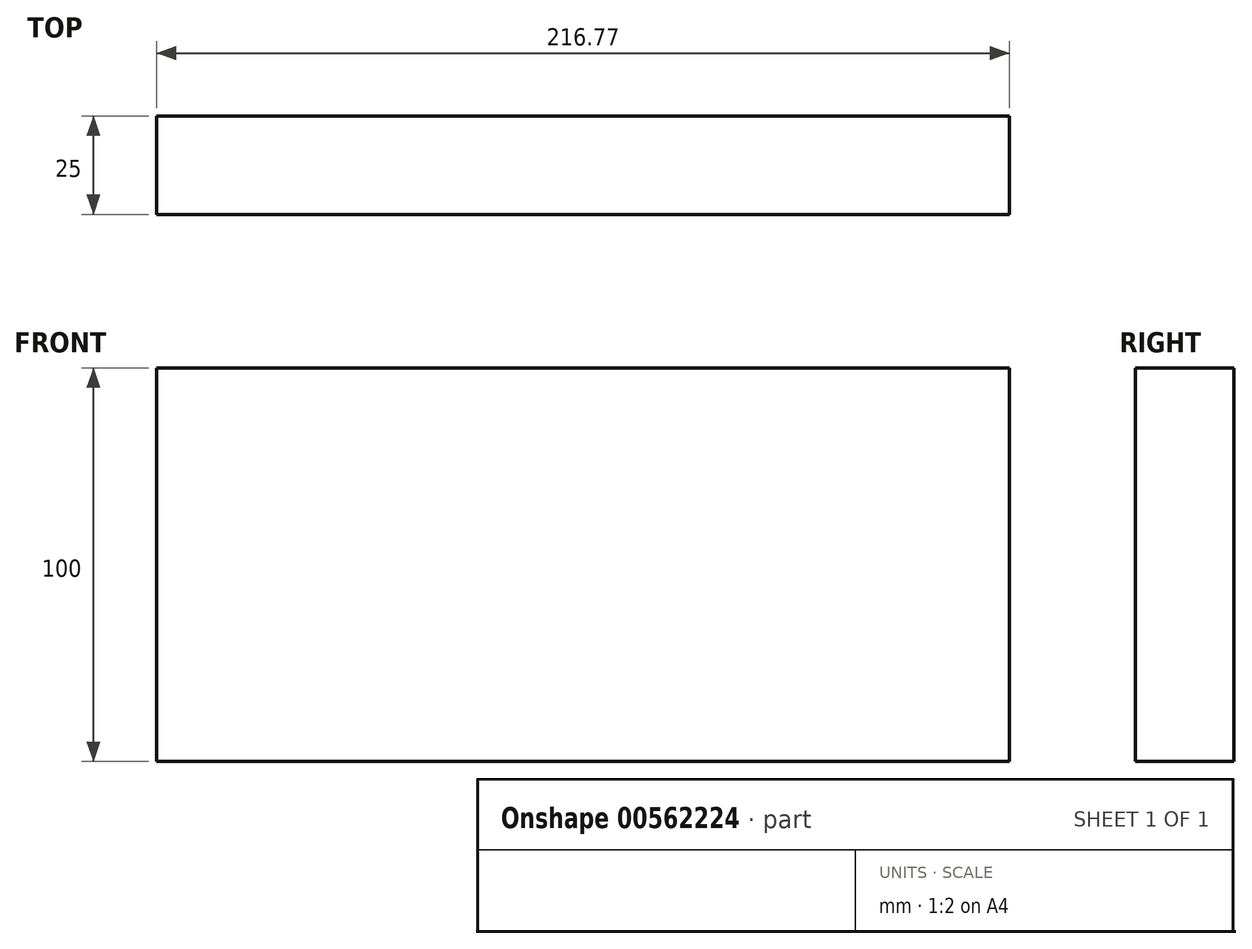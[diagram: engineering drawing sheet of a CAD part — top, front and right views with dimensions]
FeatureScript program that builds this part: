
annotation { "Feature Type Name" : "Feature", "Feature Type Description" : "" }
export const myFeature = defineFeature(function(context is Context, id is Id, definition is map)
    precondition{}
    {
        {
            var Q0;
            Q0=qCreatedBy(makeId("Front.planeOp"),FACE);
            var sketch = newSketch(context, id + "F0", { "sketchPlane" : qUnion([Q0])});
            skLineSegment(sketch, "E0.bottom", {"start": v(-124.52, 38.98) * mm, "end": v(92.25, 38.98) * mm});
            skLineSegment(sketch, "E0.top", {"start": v(-124.52, -61.02) * mm, "end": v(92.25, -61.02) * mm});
            skLineSegment(sketch, "E0.left", {"start": v(-124.52, 38.98) * mm, "end": v(-124.52, -61.02) * mm});
            skLineSegment(sketch, "E0.right", {"start": v(92.25, 38.98) * mm, "end": v(92.25, -61.02) * mm});
            skSolve(sketch);
        }
        {
            var Q0;
            Q0=makeQuery(id+"F0.imprint","IMPRINT",FACE,{"disambiguationData":[TD([[makeQuery(id+"F0.imprint","IMPRINT",EDGE,{"derivedFrom":sQuery(id+"F0.wireOp",EDGE,"E0.bottom")}),-1.0]])]});
            extrude(context, id + "F1", {"entities" : qUnion([Q0]), "depth" : 25 * mm, "offsetDistance" : 25 * mm});
        }
    });
